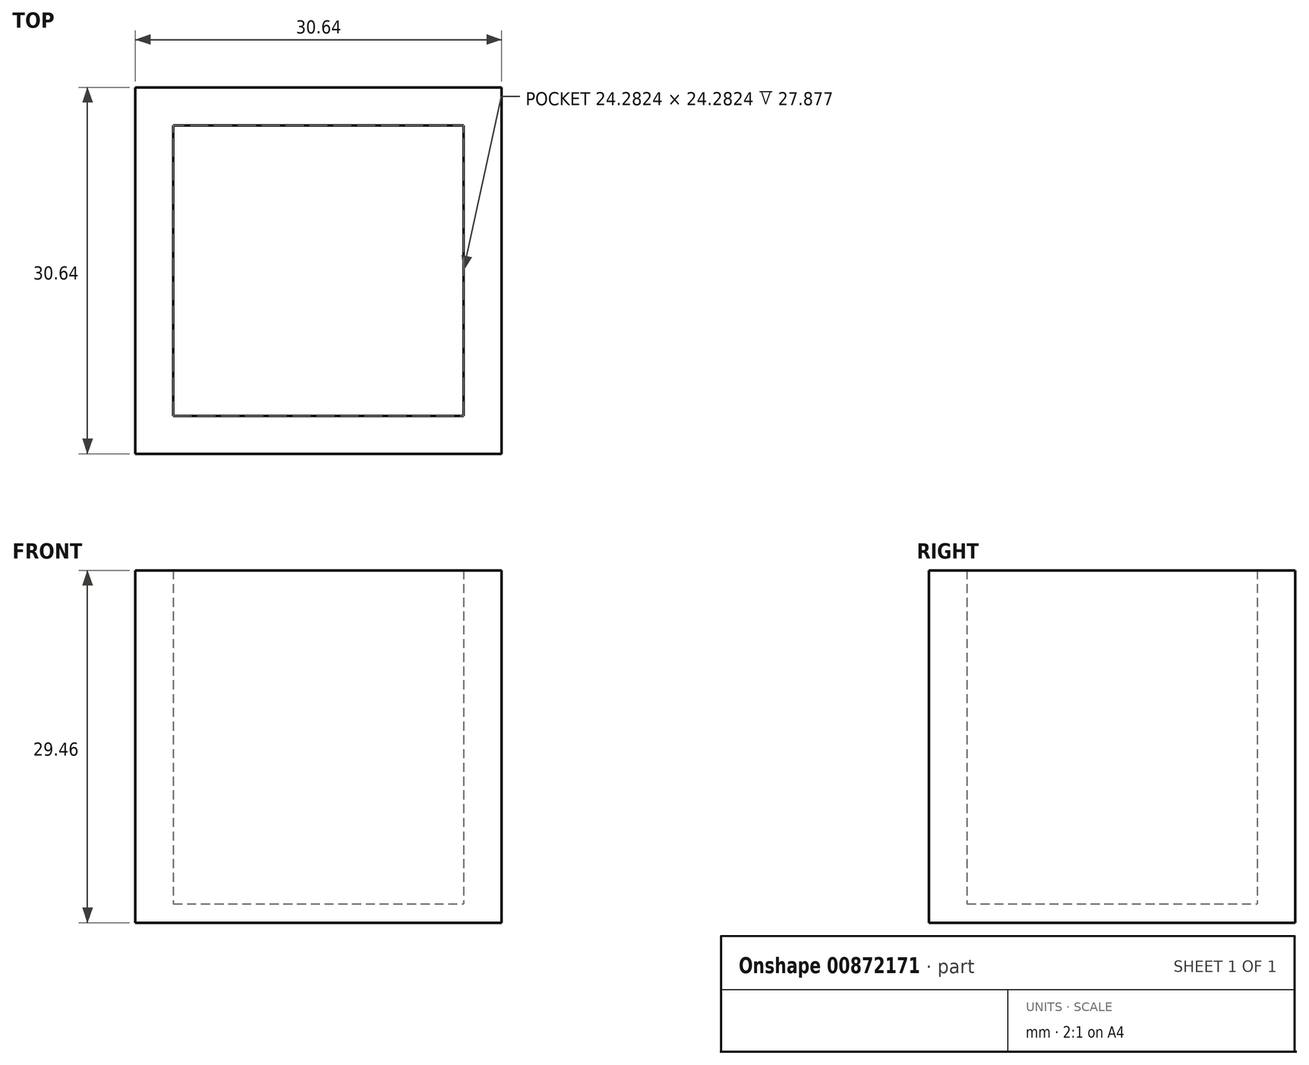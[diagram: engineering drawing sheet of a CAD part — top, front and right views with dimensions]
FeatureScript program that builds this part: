
annotation { "Feature Type Name" : "Feature", "Feature Type Description" : "" }
export const myFeature = defineFeature(function(context is Context, id is Id, definition is map)
    precondition{}
    {
        {
            var Q0;
            Q0=qCreatedBy(makeId("Top.planeOp"),FACE);
            var sketch = newSketch(context, id + "F0", { "sketchPlane" : qUnion([Q0])});
            skLineSegment(sketch, "E0.bottom", {"start": v(15.32, 15.32) * mm, "end": v(-15.32, 15.32) * mm});
            skLineSegment(sketch, "E0.top", {"start": v(15.32, -15.32) * mm, "end": v(-15.32, -15.32) * mm});
            skLineSegment(sketch, "E0.left", {"start": v(15.32, 15.32) * mm, "end": v(15.32, -15.32) * mm});
            skLineSegment(sketch, "E0.right", {"start": v(-15.32, 15.32) * mm, "end": v(-15.32, -15.32) * mm});
            skPoint(sketch, "E0.middle", {"position": v(0, 0) * mm});
            skLineSegment(sketch, "E1.0", {"start": v(12.14, -12.14) * mm, "end": v(-12.14, -12.14) * mm});
            skLineSegment(sketch, "E1.1", {"start": v(12.14, 12.14) * mm, "end": v(12.14, -12.14) * mm});
            skLineSegment(sketch, "E1.2", {"start": v(12.14, 12.14) * mm, "end": v(-12.14, 12.14) * mm});
            skLineSegment(sketch, "E1.3", {"start": v(-12.14, 12.14) * mm, "end": v(-12.14, -12.14) * mm});
            skSolve(sketch);
        }
        {
            var Q0;
            Q0=makeQuery(id+"F0.imprint","IMPRINT",FACE,{"disambiguationData":[TD([[makeQuery(id+"F0.imprint","IMPRINT",EDGE,{"derivedFrom":sQuery(id+"F0.wireOp",EDGE,"E0.bottom")}),1.0]])]});
            var Q1;
            Q1=makeQuery(id+"F0.imprint","IMPRINT",FACE,{"disambiguationData":[TD([[makeQuery(id+"F0.imprint","IMPRINT",EDGE,{"derivedFrom":sQuery(id+"F0.wireOp",EDGE,"E1.0")}),-1.0]])]});
            extrude(context, id + "F1", {"entities" : qUnion([Q0, Q1]), "depth" : 1.59 * mm, "offsetDistance" : 25 * mm});
        }
        {
            var Q0;
            Q0=makeQuery(id+"F0.imprint","IMPRINT",FACE,{"disambiguationData":[TD([[makeQuery(id+"F0.imprint","IMPRINT",EDGE,{"derivedFrom":sQuery(id+"F0.wireOp",EDGE,"E0.bottom")}),1.0]])]});
            extrude(context, id + "F2", {"entities" : qUnion([Q0]), "operationType" : NewBodyOperationType.ADD, "depth" : 29.46 * mm, "offsetDistance" : 25 * mm});
        }
    });
